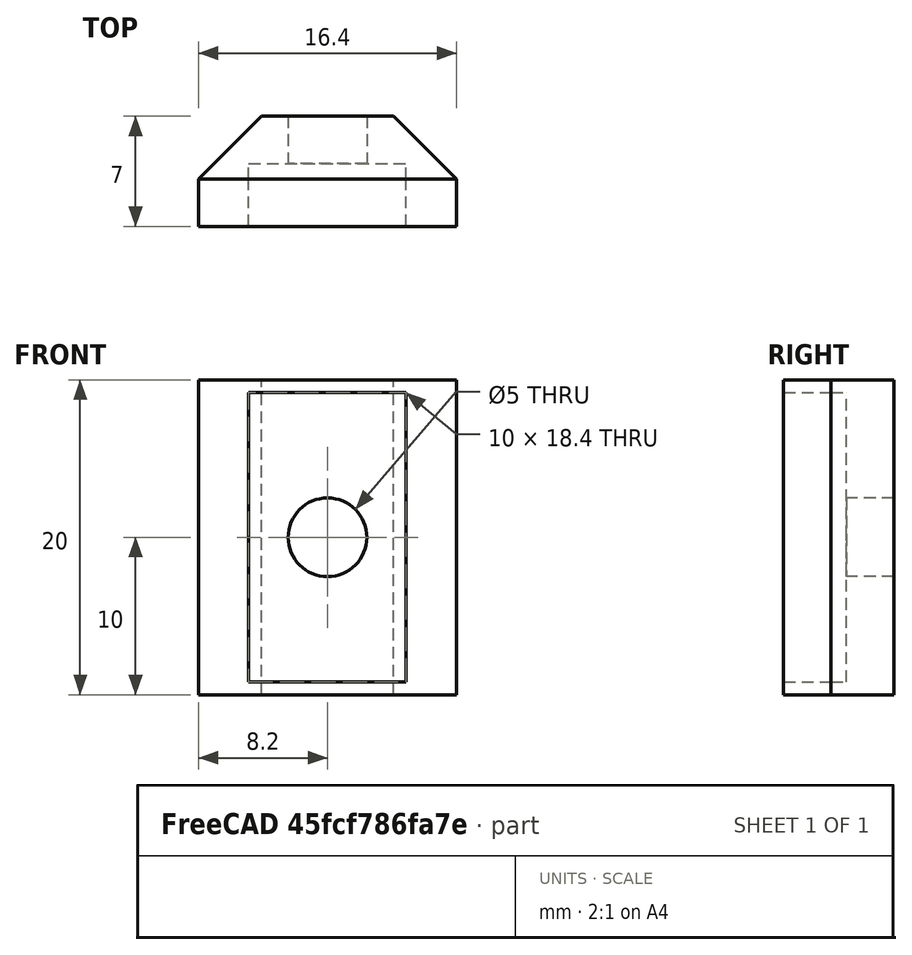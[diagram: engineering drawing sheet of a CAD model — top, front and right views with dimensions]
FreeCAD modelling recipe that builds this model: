
FCSTD DOCUMENT  (FreeCAD 0.19R24276 (Git))
Label: T-hold_max_001
License: All rights reserved
LicenseURL: http://en.wikipedia.org/wiki/All_rights_reserved
objects: Part::Cut×5, Part::Cylinder×3, Part::Box×3, Mesh::Feature×2, Part::Wedge×1, Part::Compound×1
note: 13 computed .brp shape members not serialized (recipe doc carries the construction recipe); baked Part::Feature solids carry a one-line shape summary decoded from their .brp

FEATURE [Part::Wedge] Wedge  label="Klín"
  AttacherType = Attacher::AttachEngine3D
  Placement = pos=(-8.2,1.5,-10) rot=(0,0,1;0rad)
  X2max = 12.4
  X2min = 4
  Xmax = 16.4
  Xmin = 0
  Ymax = 4
  Ymin = 0
  Z2max = 20
  Z2min = 0
  Zmax = 20
  Zmin = 0
FEATURE [Part::Cylinder] Cylinder002  label="Válec002"
  Angle = 360
  AttacherType = Attacher::AttachEngine3D
  Height = 10
  Placement = pos=(0,7,0) rot=(1,0,0;1.5708rad)
  Radius = 2.5
FEATURE [Part::Cylinder] Cylinder001  label="Válec001"
  Angle = 360
  AttacherType = Attacher::AttachEngine3D
  Height = 10
  Placement = pos=(0,7,0) rot=(1,0,0;1.5708rad)
  Radius = 2.5
FEATURE [Part::Cylinder] Cylinder  label="Válec"
  Angle = 360
  AttacherType = Attacher::AttachEngine3D
  Height = 10
  Placement = pos=(0,7,0) rot=(1,0,0;1.5708rad)
  Radius = 2.5
FEATURE [Part::Box] Box002  label="Krychle002"
  AttacherType = Attacher::AttachEngine3D
  Height = 18.4
  Length = 10
  Placement = pos=(-5,-1.5,-9.2) rot=(0,0,1;0rad)
  Width = 4
FEATURE [Part::Box] Box  label="Krychle"
  AttacherType = Attacher::AttachEngine3D
  Height = 20
  Length = 16.4
  Placement = pos=(-8.2,-1.5,-10) rot=(0,0,1;0rad)
  Width = 3
FEATURE [Part::Cut] Cut001
  Base = -> Box
  Tool = -> Box002
FEATURE [Part::Cut] Cut002
  Base = -> Cut001
  Tool = -> Cylinder
FEATURE [Part::Cut] Cut003
  Base = -> Cut002
  Tool = -> Cylinder001
FEATURE [Part::Box] Box001  label="Krychle001"
  AttacherType = Attacher::AttachEngine3D
  Height = 18.4
  Length = 10
  Placement = pos=(-5,-1.5,-9.2) rot=(0,0,1;0rad)
  Width = 4
FEATURE [Part::Cut] Cut
  Base = -> Wedge
  Tool = -> Box001
FEATURE [Part::Compound] Compound  label="teckovka"
  Links = -> [Cut,Cut003]
FEATURE [Part::Cut] Cut004  label="T-hold_max"
  Base = -> Compound
  Tool = -> Cylinder002
FEATURE [Mesh::Feature] Mesh  label="teckovy_bigo_drzacek (Meshed)"
FEATURE [Mesh::Feature] Mesh001  label="T-hold_max (Meshed)"
